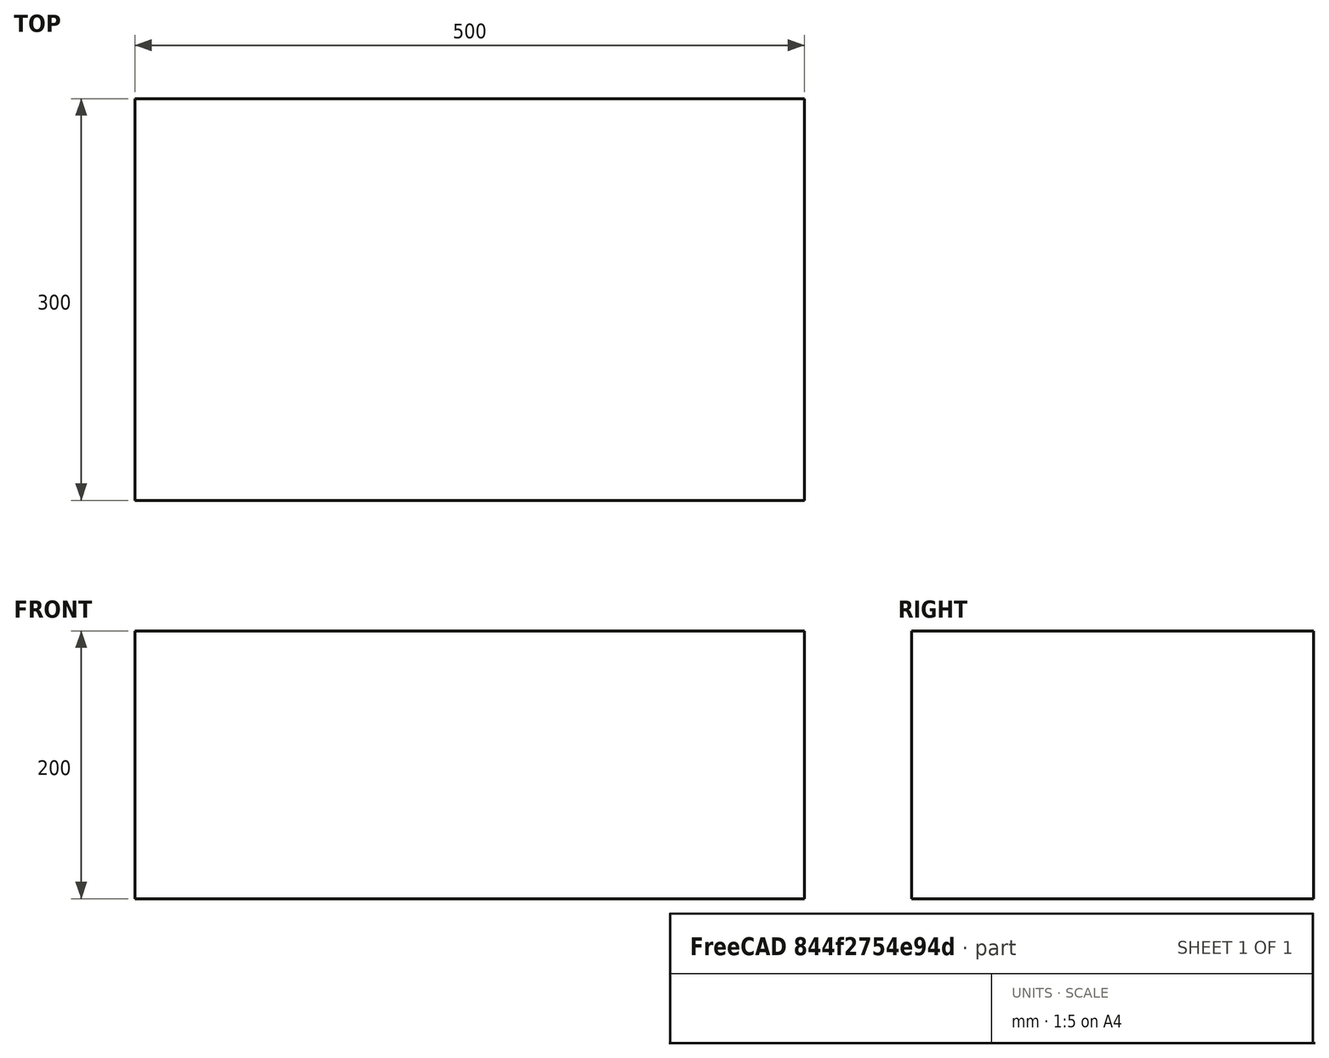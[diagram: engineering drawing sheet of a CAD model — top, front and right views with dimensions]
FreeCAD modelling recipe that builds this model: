
FCSTD DOCUMENT  (FreeCAD 0.21R33771 (Git))
Label: part1(box)
License: All rights reserved
LicenseURL: http://en.wikipedia.org/wiki/All_rights_reserved
objects: Sketcher::SketchObject×1, PartDesign::Pad×1, PartDesign::Body×1
note: 4 computed .brp shape members not serialized (recipe doc carries the construction recipe); baked Part::Feature solids carry a one-line shape summary decoded from their .brp

FEATURE [Sketcher::SketchObject] Sketch
  FullyConstrained = true
  MapMode = 5
  Support = -> [XY_Plane]
  sketch-geometry (5):
    g0: LineSegment StartX=-250 StartY=-150 StartZ=0 EndX=-250 EndY=150 EndZ=0
    g1: LineSegment StartX=-250 StartY=150 StartZ=0 EndX=250 EndY=150 EndZ=0
    g2: LineSegment StartX=250 StartY=150 StartZ=0 EndX=250 EndY=-150 EndZ=0
    g3: LineSegment StartX=250 StartY=-150 StartZ=0 EndX=-250 EndY=-150 EndZ=0
    g4: GeomPoint X=0 Y=0 Z=0
  constraints (12):
    c: Coincident(g0,g1)
    c: Coincident(g1,g2)
    c: Coincident(g2,g3)
    c: Coincident(g3,g0)
    c: Horizontal(g1)
    c: Horizontal(g3)
    c: Vertical(g0)
    c: Vertical(g2)
    c: Symmetric(g1,g0,g4)
    c: Coincident(g4,g-1)
    c: DistanceX(g1,g1) = 500
    c: DistanceY(g0,g0) = 300
FEATURE [PartDesign::Pad] Pad
  Direction = (0,0,1)
  Length = 200
  Length2 = 10
  Profile = -> Sketch
  ReferenceAxis = -> Sketch [N_Axis]
  Type = 0
FEATURE [PartDesign::Body] Body
  Group = -> [Sketch,Pad]
  Origin = -> Origin
  Tip = -> Pad
